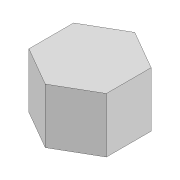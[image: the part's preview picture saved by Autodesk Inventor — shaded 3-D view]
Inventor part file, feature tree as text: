
AUTODESK INVENTOR PART (.ipt)
format: ipt  version: 2022 (Build 260153000, 153)  size: 77,312 bytes
history: native  units: mm
features: extrude x1, sketch x1
ambient origin geometry x8: Origin, YZ Plane, XZ Plane, XY Plane, X Axis, Y Axis, Z Axis, Center Point
bodies: Solid1 (feature_tree)
feature tree (2):
  extrude  "Extrusion1"  Depth=4.9mm TaperAngle=0.0deg
  sketch  "Sketch1"  dims[d0=6.9mm d1=4.9mm d2=0.0mm]
